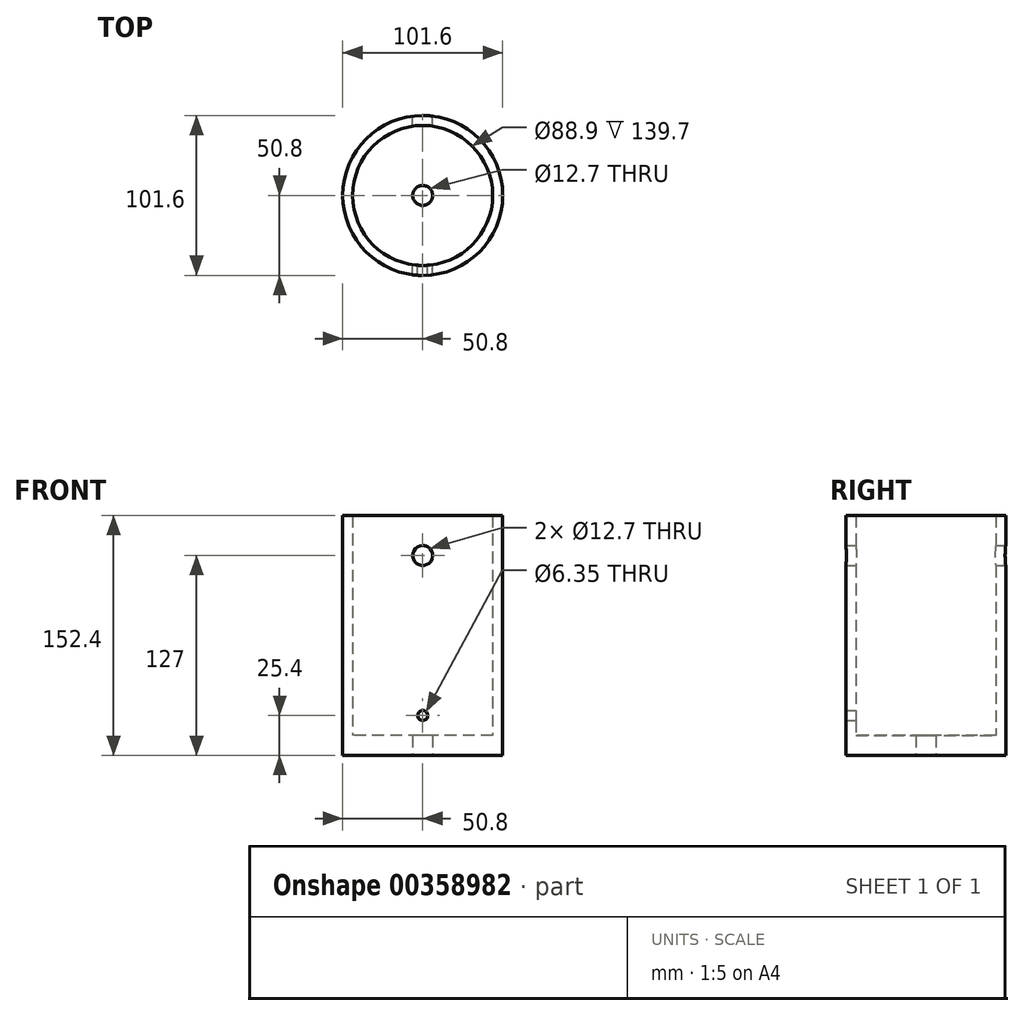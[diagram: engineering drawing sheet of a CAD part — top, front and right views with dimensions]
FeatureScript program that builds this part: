
annotation { "Feature Type Name" : "Feature", "Feature Type Description" : "" }
export const myFeature = defineFeature(function(context is Context, id is Id, definition is map)
    precondition{}
    {
        {
            var Q0;
            Q0=qCreatedBy(makeId("Top.planeOp"),FACE);
            var sketch = newSketch(context, id + "F0", { "sketchPlane" : qUnion([Q0])});
            skCircle(sketch, "E0", {"center": v(0, 0) * mm, "radius": 50.8 * mm});
            skCircle(sketch, "E1", {"center": v(0, 0) * mm, "radius": 44.45 * mm});
            skCircle(sketch, "E2", {"center": v(0, 0) * mm, "radius": 6.35 * mm});
            skSolve(sketch);
        }
        {
            var Q0;
            Q0 = qSketchRegion(id + "F0", true);
            extrude(context, id + "F1", {"entities" : qUnion([Q0]), "depth" : 152.4 * mm});
        }
        {
            var Q0;
            Q0=makeQuery(id+"F0.imprint","IMPRINT",FACE,{"disambiguationData":[TD([[makeQuery(id+"F0.imprint","IMPRINT",EDGE,{"derivedFrom":sQuery(id+"F0.wireOp",EDGE,"E1")}),1.0]])]});
            var Q1;
            Q1 = qSketchRegion(id + "F0", true);
            extrude(context, id + "F2", {"entities" : qUnion([Q0, Q1]), "operationType" : NewBodyOperationType.ADD, "depth" : 12.7 * mm});
        }
        {
            var Q0;
            Q0=qCreatedBy(makeId("Front.planeOp"),FACE);
            var sketch = newSketch(context, id + "F3", { "sketchPlane" : qUnion([Q0])});
            skCircle(sketch, "E3", {"center": v(0, 25.4) * mm, "radius": 3.18 * mm});
            skCircle(sketch, "E4", {"center": v(0, 127) * mm, "radius": 6.35 * mm});
            skSolve(sketch);
        }
        {
            var Q0;
            Q0=makeQuery(id+"F3.imprint","IMPRINT",FACE,{"disambiguationData":[TD([[makeQuery(id+"F3.imprint","IMPRINT",EDGE,{"derivedFrom":sQuery(id+"F3.wireOp",EDGE,"E4")}),1.0]])]});
            extrude(context, id + "F4", {"entities" : qUnion([Q0]), "operationType" : NewBodyOperationType.REMOVE, "depth" : 127 * mm, "symmetric" : true});
        }
        {
            var Q0;
            Q0=makeQuery(id+"F3.imprint","IMPRINT",FACE,{"disambiguationData":[TD([[makeQuery(id+"F3.imprint","IMPRINT",EDGE,{"derivedFrom":sQuery(id+"F3.wireOp",EDGE,"E3")}),1.0]])]});
            extrude(context, id + "F5", {"entities" : qUnion([Q0]), "operationType" : NewBodyOperationType.REMOVE, "endBound" : BoundingType.THROUGH_ALL, "depth" : 152.4 * mm});
        }
    });
